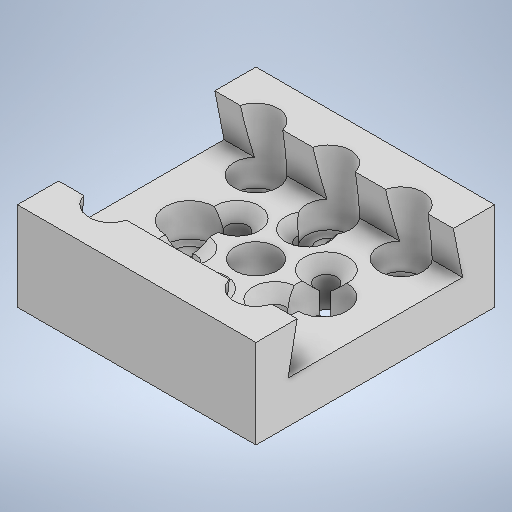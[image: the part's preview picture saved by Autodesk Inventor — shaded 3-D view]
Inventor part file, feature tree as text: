
AUTODESK INVENTOR PART (.ipt)
format: ipt  version: 2025 (Build 290162000, 162)  size: 424,960 bytes
history: native  units: mm
features: sketch x11, extrude x9, chamfer x1
ambient origin geometry x8: Origin, YZ Plane, XZ Plane, XY Plane, X Axis, Y Axis, Z Axis, Center Point
bodies: Solid1 (feature_tree)
feature tree (21):
  extrude  "Extrusion1"  Depth=62.6mm
  extrude  "Extrusion3"  Depth=31.3mm
  sketch  "Sketch4"  dims[d8=30.0mm d10=19.05mm d11=20.0mm d13=38.1mm d16=11.0mm d17=0.0mm]
  extrude  "Extrusion4"  Depth=19.05mm
  extrude  "Extrusion5"  Depth=6.2mm
  extrude  "Extrusion6"  Depth=11.0mm TaperAngle=0.0deg
  extrude  "Extrusion7"  Depth=31.3mm
  extrude  "Extrusion8"  Depth=11.0mm TaperAngle=0.0deg
  chamfer  "Chamfer3"  Distance=11.5mm
  extrude  "Extrusion9"  Depth=12.3mm
  extrude  "Extrusion10"  Depth=7.0mm TaperAngle=0.0deg
  sketch  "Sketch1"  dims[d0=62.6mm d1=62.6mm]
  sketch  "Sketch Rectangular Pattern1"  dims[d2=5.0mm d3=31.3mm]
  sketch  "Sketch3"  dims[d4=31.3mm d5=19.05mm]
  sketch  "Sketch5"  dims[d47=5.0mm d48=31.3mm]
  sketch  "Sketch7"  dims[d49=31.3mm d50=11.0mm d51=0.0mm]
  sketch  "Sketch8"  dims[d52=11.0mm]
  sketch  "Sketch9"  dims[d53=11.5mm]
  sketch  "Sketch Circular Pattern3"  dims[d6=19.05mm d7=6.2mm]
  sketch  "Sketch10"  dims[d54=11.5mm]
  sketch  "Sketch11"  dims[d55=11.5mm d56=11.5mm d57=11.5mm d58=7.0mm d59=0.0mm d61=8.0mm d62=0.0mm d63=2.0mm d64=8.1mm d65=17.4mm d66=8.1mm d67=17.4mm d68=11.0mm d69=0.0mm d70=12.8mm d71=12.8mm d72=8.7mm d73=0.0mm d86=2.0mm d87=31.3mm d88=31.3mm d89=5.5mm d90=13.5mm d91=60.0mm d93=360.0deg d95=11.0mm d96=0.0mm d97=3.0mm d98=2.0mm d99=45.0deg d100=12.3mm d101=10.8mm d102=8.4mm d103=12.3mm d104=10.8mm d105=8.4mm d106=62.6mm d107=0.0mm d108=62.6mm d109=0.0mm d82=0.5mm d83=0.872665mm d84=0.5mm d85=0.872665mm]
